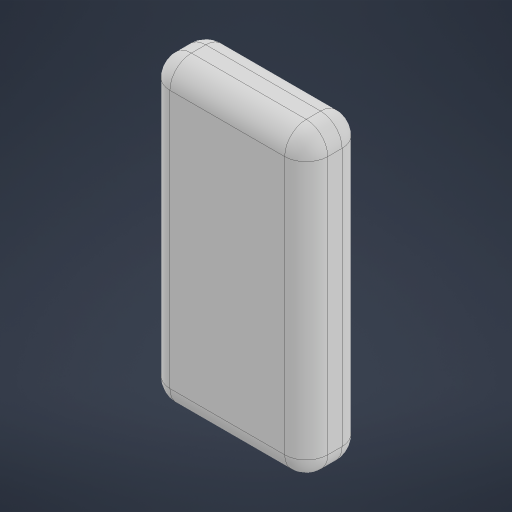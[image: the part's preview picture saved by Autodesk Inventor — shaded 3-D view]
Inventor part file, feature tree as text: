
AUTODESK INVENTOR PART (.ipt)
format: ipt  version: 2023 (Build 270158000, 158)  size: 185,856 bytes
history: native  units: in
note: dims shown in document units (in); Inventor stores cm internally (conversion verified against a paired STEP export)
features: extrude x1, fillet x1, sketch x1
ambient origin geometry x8: Origin, YZ Plane, XZ Plane, XY Plane, X Axis, Y Axis, Z Axis, Center Point
bodies: Solid1 (feature_tree)
feature tree (3):
  extrude  "Extrusion1"  Depth=5.25in
  fillet  "Fillet1"  Radius=1.0in
  sketch  "Sketch1"  dims[d0=2.75in d1=5.25in d2=1.0in d3=0.0in d4=0.375in]
